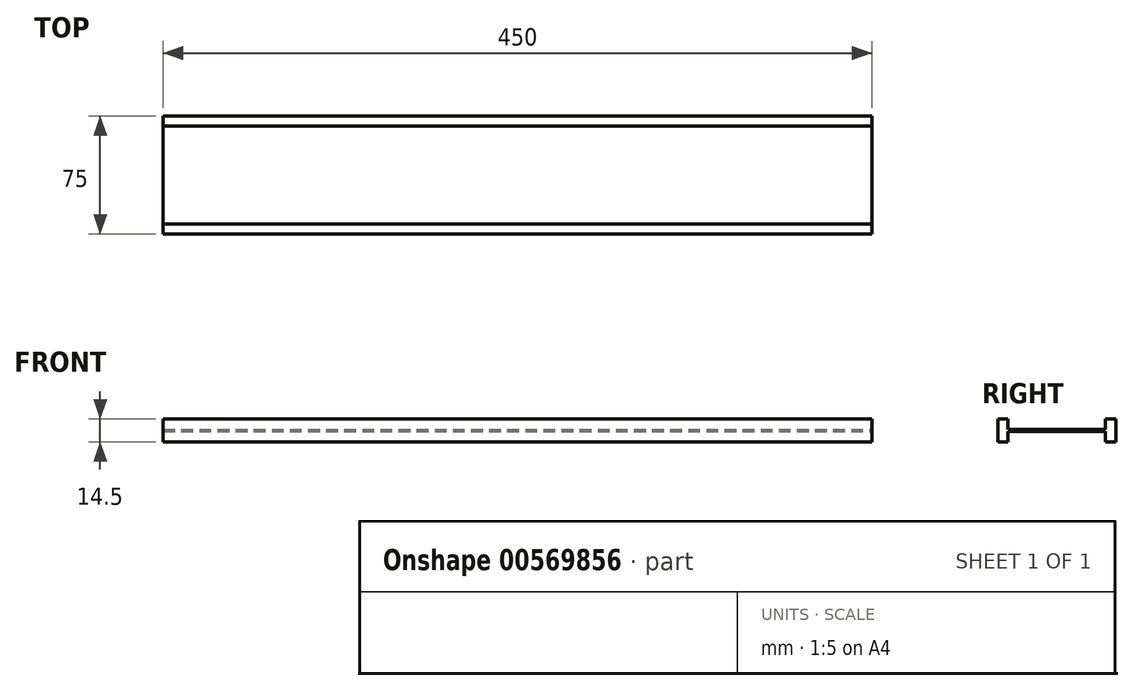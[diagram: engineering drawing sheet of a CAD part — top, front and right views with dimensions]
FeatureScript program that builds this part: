
annotation { "Feature Type Name" : "Feature", "Feature Type Description" : "" }
export const myFeature = defineFeature(function(context is Context, id is Id, definition is map)
    precondition{}
    {
        {
            var Q0;
            Q0=qCreatedBy(makeId("Top.planeOp"),FACE);
            var sketch = newSketch(context, id + "F0", { "sketchPlane" : qUnion([Q0])});
            skLineSegment(sketch, "E0.bottom", {"start": v(225, 37.5) * mm, "end": v(-225, 37.5) * mm});
            skLineSegment(sketch, "E0.top", {"start": v(225, -37.5) * mm, "end": v(-225, -37.5) * mm});
            skLineSegment(sketch, "E0.left", {"start": v(225, 37.5) * mm, "end": v(225, -37.5) * mm});
            skLineSegment(sketch, "E0.right", {"start": v(-225, 37.5) * mm, "end": v(-225, -37.5) * mm});
            skPoint(sketch, "E0.middle", {"position": v(0, 0) * mm});
            skSolve(sketch);
        }
        {
            var Q0;
            Q0 = qSketchRegion(id + "F0", true);
            extrude(context, id + "F1", {"entities" : qUnion([Q0]), "depth" : 1.5 * mm, "offsetDistance" : 25.4 * mm});
        }
        {
            var Q0;
            Q0=makeQuery(id+"F1.opExtrude","CAP_FACE",FACE,{"disambiguationData":[OSD([sQuery(id+"F0.wireOp",EDGE,"E0.bottom"),sQuery(id+"F0.wireOp",EDGE,"E0.top"),sQuery(id+"F0.wireOp",EDGE,"E0.left"),sQuery(id+"F0.wireOp",EDGE,"E0.right")])],"isStart":false});
            var sketch = newSketch(context, id + "F2", { "sketchPlane" : qUnion([Q0])});
            skLineSegment(sketch, "E1.bottom", {"start": v(-225, 37.5) * mm, "end": v(225, 37.5) * mm});
            skLineSegment(sketch, "E1.top", {"start": v(-225, 31) * mm, "end": v(225, 31) * mm});
            skLineSegment(sketch, "E1.left", {"start": v(-225, 37.5) * mm, "end": v(-225, 31) * mm});
            skLineSegment(sketch, "E1.right", {"start": v(225, 37.5) * mm, "end": v(225, 31) * mm});
            skLineSegment(sketch, "E2.bottom", {"start": v(-225, -37.5) * mm, "end": v(225, -37.5) * mm});
            skLineSegment(sketch, "E2.top", {"start": v(-225, -31) * mm, "end": v(225, -31) * mm});
            skLineSegment(sketch, "E2.left", {"start": v(-225, -37.5) * mm, "end": v(-225, -31) * mm});
            skLineSegment(sketch, "E2.right", {"start": v(225, -37.5) * mm, "end": v(225, -31) * mm});
            skSolve(sketch);
        }
        {
            var Q0;
            Q0=makeQuery(id+"F2.imprint","IMPRINT",FACE,{"disambiguationData":[TD([[makeQuery(id+"F2.imprint","IMPRINT",EDGE,{"derivedFrom":sQuery(id+"F2.wireOp",EDGE,"E2.bottom")}),-1.0]])]});
            var Q1;
            Q1=makeQuery(id+"F2.imprint","IMPRINT",FACE,{"disambiguationData":[TD([[makeQuery(id+"F2.imprint","IMPRINT",EDGE,{"derivedFrom":sQuery(id+"F2.wireOp",EDGE,"E1.bottom")}),1.0]])]});
            extrude(context, id + "F3", {"entities" : qUnion([Q0, Q1]), "operationType" : NewBodyOperationType.ADD, "depth" : 6.5 * mm, "offsetDistance" : 25.4 * mm});
        }
        {
            var Q0;
            Q0=makeQuery(id+"F1.opExtrude","CAP_FACE",FACE,{"disambiguationData":[OSD([sQuery(id+"F0.wireOp",EDGE,"E0.bottom"),sQuery(id+"F0.wireOp",EDGE,"E0.top"),sQuery(id+"F0.wireOp",EDGE,"E0.left"),sQuery(id+"F0.wireOp",EDGE,"E0.right")])],"isStart":true});
            var sketch = newSketch(context, id + "F4", { "sketchPlane" : qUnion([Q0])});
            skLineSegment(sketch, "E3.bottom", {"start": v(-225, 37.5) * mm, "end": v(225, 37.5) * mm});
            skLineSegment(sketch, "E3.top", {"start": v(-225, 31) * mm, "end": v(225, 31) * mm});
            skLineSegment(sketch, "E3.left", {"start": v(-225, 37.5) * mm, "end": v(-225, 31) * mm});
            skLineSegment(sketch, "E3.right", {"start": v(225, 37.5) * mm, "end": v(225, 31) * mm});
            skLineSegment(sketch, "E4.bottom", {"start": v(-225, -37.5) * mm, "end": v(225, -37.5) * mm});
            skLineSegment(sketch, "E4.top", {"start": v(-225, -31) * mm, "end": v(225, -31) * mm});
            skLineSegment(sketch, "E4.left", {"start": v(-225, -37.5) * mm, "end": v(-225, -31) * mm});
            skLineSegment(sketch, "E4.right", {"start": v(225, -37.5) * mm, "end": v(225, -31) * mm});
            skSolve(sketch);
        }
        {
            var Q0;
            Q0 = qSketchRegion(id + "F4", true);
            extrude(context, id + "F5", {"entities" : qUnion([Q0]), "operationType" : NewBodyOperationType.ADD, "depth" : 6.5 * mm, "offsetDistance" : 25.4 * mm});
        }
    });
